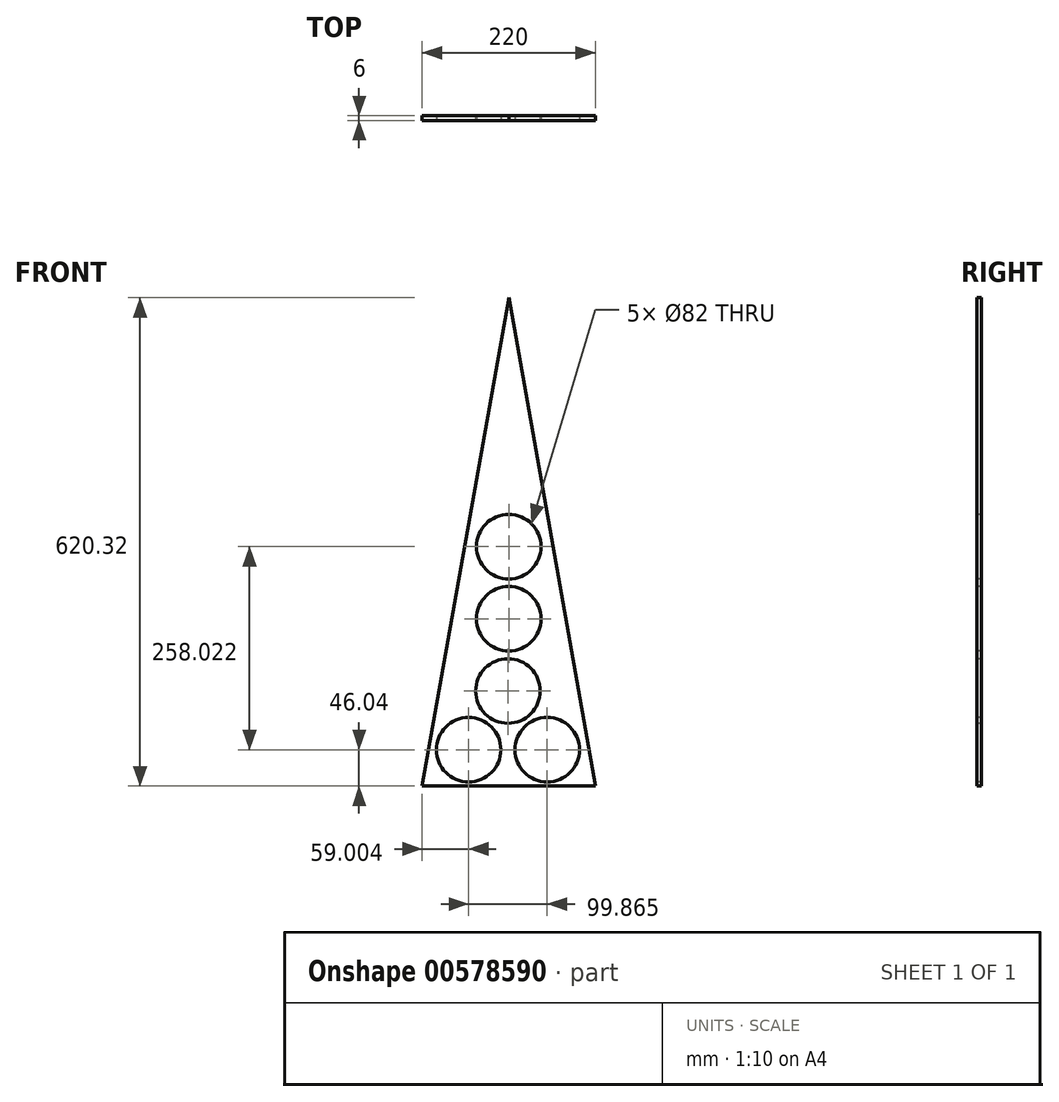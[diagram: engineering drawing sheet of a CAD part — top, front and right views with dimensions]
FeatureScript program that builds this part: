
annotation { "Feature Type Name" : "Feature", "Feature Type Description" : "" }
export const myFeature = defineFeature(function(context is Context, id is Id, definition is map)
    precondition{}
    {
        {
            var Q0;
            Q0=qCreatedBy(makeId("Front.planeOp"),FACE);
            var sketch = newSketch(context, id + "F0", { "sketchPlane" : qUnion([Q0])});
            skLineSegment(sketch, "E0", {"start": v(0, 261.15) * mm, "end": v(-110, -359.17) * mm});
            skLineSegment(sketch, "E1", {"start": v(-110, -359.17) * mm, "end": v(110, -359.17) * mm});
            skLineSegment(sketch, "E2", {"start": v(110, -359.17) * mm, "end": v(0, 261.15) * mm});
            skSolve(sketch);
        }
        {
            var Q0;
            Q0 = qSketchRegion(id + "F0", true);
            extrude(context, id + "F1", {"entities" : qUnion([Q0]), "depth" : 6 * mm, "offsetDistance" : 25.4 * mm});
        }
        {
            var Q0;
            Q0=makeQuery(id+"F1.opExtrude","CAP_FACE",FACE,{"disambiguationData":[OSD([sQuery(id+"F0.wireOp",EDGE,"E0"),sQuery(id+"F0.wireOp",EDGE,"E1"),sQuery(id+"F0.wireOp",EDGE,"E2")])],"isStart":false});
            var sketch = newSketch(context, id + "F2", { "sketchPlane" : qUnion([Q0])});
            skCircle(sketch, "E3", {"center": v(48.87, -313.13) * mm, "radius": 41 * mm});
            skCircle(sketch, "E4", {"center": v(-51, -313.13) * mm, "radius": 41 * mm});
            skCircle(sketch, "E5", {"center": v(-1.12, -238.52) * mm, "radius": 41 * mm});
            skCircle(sketch, "E6", {"center": v(0, -146.75) * mm, "radius": 41 * mm});
            skCircle(sketch, "E7", {"center": v(0, -55.1) * mm, "radius": 41 * mm});
            skSolve(sketch);
        }
        {
            var Q0;
            Q0 = qSketchRegion(id + "F2", true);
            extrude(context, id + "F3", {"entities" : qUnion([Q0]), "operationType" : NewBodyOperationType.REMOVE, "oppositeDirection" : true, "depth" : 164.34 * mm, "offsetDistance" : 25.4 * mm});
        }
    });
